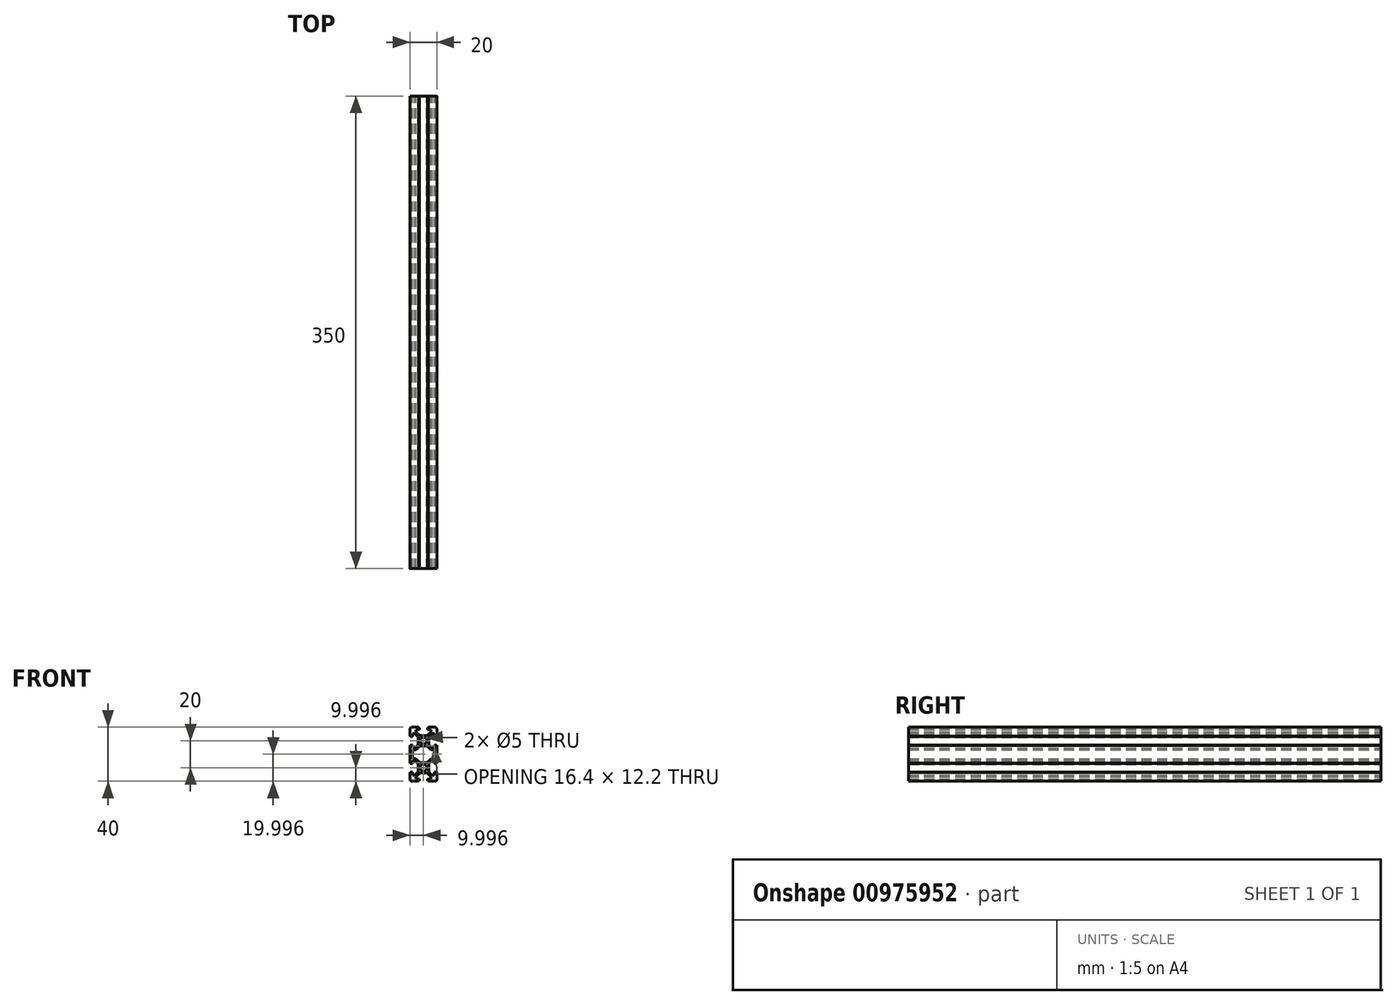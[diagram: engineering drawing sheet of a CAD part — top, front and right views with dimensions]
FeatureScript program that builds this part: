
annotation { "Feature Type Name" : "Feature", "Feature Type Description" : "" }
export const myFeature = defineFeature(function(context is Context, id is Id, definition is map)
    precondition{}
    {
        {
            var Q0;
            Q0=qCreatedBy(makeId("Front.planeOp"),FACE);
            var sketch = newSketch(context, id + "F0", { "sketchPlane" : qUnion([Q0])});
            skCircle(sketch, "E0", {"center": v(-97.48, 54.07) * mm, "radius": 2.5 * mm});
            skLineSegment(sketch, "E1.bottom", {"start": v(-88.98, 44.07) * mm, "end": v(-93.38, 44.07) * mm});
            skLineSegment(sketch, "E1.left", {"start": v(-87.48, 45.57) * mm, "end": v(-87.48, 50.47) * mm});
            skLineSegment(sketch, "E2.bottom", {"start": v(-95.47, 50.17) * mm, "end": v(-99.5, 50.17) * mm});
            skLineSegment(sketch, "E2.top", {"start": v(-95.47, 57.97) * mm, "end": v(-99.5, 57.97) * mm});
            skLineSegment(sketch, "E2.left", {"start": v(-93.58, 52.06) * mm, "end": v(-93.58, 56.08) * mm});
            skLineSegment(sketch, "E2.right", {"start": v(-101.38, 52.06) * mm, "end": v(-101.38, 56.08) * mm});
            skLineSegment(sketch, "E3.left", {"start": v(-87.48, 62.57) * mm, "end": v(-87.48, 59.57) * mm});
            skLineSegment(sketch, "E4", {"start": v(-93, 57.5) * mm, "end": v(-90.92, 59.57) * mm});
            skLineSegment(sketch, "E5.MirrorCS", {"start": v(-94.06, 58.55) * mm, "end": v(-91.98, 60.63) * mm});
            skLineSegment(sketch, "E6", {"start": v(-89.28, 59.57) * mm, "end": v(-89.28, 57.17) * mm});
            skLineSegment(sketch, "E7", {"start": v(-87.78, 57.67) * mm, "end": v(-87.48, 57.67) * mm});
            skLineSegment(sketch, "E8", {"start": v(-89.28, 57.17) * mm, "end": v(-87.98, 57.17) * mm});
            skLineSegment(sketch, "E9", {"start": v(-87.98, 57.47) * mm, "end": v(-87.98, 57.17) * mm});
            skPoint(sketch, "E10.visualSharp", {"position": v(-87.98, 57.67) * mm});
            skArc(sketch, "E10.filletArc", {"start": v(-87.78, 57.67) * mm, "mid": v(-87.93, 57.6) * mm, "end": v(-87.98, 57.47) * mm});
            skPoint(sketch, "E11.newPointA", {"position": v(-93.58, 56.9) * mm});
            skArc(sketch, "E11.filletArc", {"start": v(-93, 57.5) * mm, "mid": v(-93.43, 56.84) * mm, "end": v(-93.58, 56.08) * mm});
            skPoint(sketch, "E12.newPointA", {"position": v(-94.65, 57.97) * mm});
            skPoint(sketch, "E12.newPointB", {"position": v(-93.58, 57.97) * mm});
            skArc(sketch, "E12.filletArc", {"start": v(-95.47, 57.97) * mm, "mid": v(-94.7, 58.12) * mm, "end": v(-94.06, 58.55) * mm});
            skLineSegment(sketch, "E13.trimOffspring", {"start": v(-89.28, 59.57) * mm, "end": v(-90.92, 59.57) * mm});
            skLineSegment(sketch, "E14.MirrorCS", {"start": v(-87.78, 50.47) * mm, "end": v(-87.48, 50.47) * mm});
            skArc(sketch, "E15.MirrorCS", {"start": v(-87.78, 50.47) * mm, "mid": v(-87.93, 50.52) * mm, "end": v(-87.98, 50.67) * mm});
            skLineSegment(sketch, "E16.MirrorCS", {"start": v(-87.98, 50.67) * mm, "end": v(-87.98, 50.97) * mm});
            skArc(sketch, "E17.MirrorCS", {"start": v(-93, 50.64) * mm, "mid": v(-93.43, 51.29) * mm, "end": v(-93.58, 52.06) * mm});
            skLineSegment(sketch, "E18.MirrorCS", {"start": v(-89.28, 48.57) * mm, "end": v(-90.92, 48.57) * mm});
            skLineSegment(sketch, "E19.MirrorCS", {"start": v(-89.28, 50.97) * mm, "end": v(-87.98, 50.97) * mm});
            skLineSegment(sketch, "E20.MirrorCS", {"start": v(-88.98, 44.07) * mm, "end": v(-91.98, 44.07) * mm});
            skPoint(sketch, "E21.MirrorP", {"position": v(-87.98, 50.47) * mm});
            skLineSegment(sketch, "E22.MirrorCS", {"start": v(-94.38, 45.87) * mm, "end": v(-94.38, 44.57) * mm});
            skLineSegment(sketch, "E23.MirrorCS", {"start": v(-91.98, 45.87) * mm, "end": v(-94.38, 45.87) * mm});
            skLineSegment(sketch, "E24.MirrorCS", {"start": v(-89.28, 48.57) * mm, "end": v(-89.28, 50.97) * mm});
            skLineSegment(sketch, "E25.MirrorCS", {"start": v(-87.48, 45.57) * mm, "end": v(-87.48, 48.57) * mm});
            skLineSegment(sketch, "E26.MirrorCS", {"start": v(-93, 50.64) * mm, "end": v(-90.92, 48.57) * mm});
            skPoint(sketch, "E27.MirrorP", {"position": v(-93.58, 51.23) * mm});
            skPoint(sketch, "E28.MirrorP", {"position": v(-87.48, 44.07) * mm});
            skPoint(sketch, "E29.MirrorP", {"position": v(-93.58, 50.17) * mm});
            skLineSegment(sketch, "E30.MirrorCS", {"start": v(-94.06, 49.58) * mm, "end": v(-91.98, 47.5) * mm});
            skPoint(sketch, "E31.MirrorP", {"position": v(-94.65, 50.17) * mm});
            skArc(sketch, "E32.MirrorCS", {"start": v(-87.48, 45.57) * mm, "mid": v(-87.92, 44.5) * mm, "end": v(-88.98, 44.07) * mm});
            skLineSegment(sketch, "E33.MirrorCS", {"start": v(-91.98, 45.87) * mm, "end": v(-91.98, 47.5) * mm});
            skArc(sketch, "E34.MirrorCS", {"start": v(-95.47, 50.17) * mm, "mid": v(-94.7, 50.01) * mm, "end": v(-94.06, 49.58) * mm});
            skLineSegment(sketch, "E35.trimOffspring", {"start": v(-87.48, 57.67) * mm, "end": v(-87.48, 62.57) * mm});
            skLineSegment(sketch, "E36.MirrorCS", {"start": v(-93.88, 44.37) * mm, "end": v(-93.88, 44.07) * mm});
            skLineSegment(sketch, "E37.MirrorCS", {"start": v(-94.08, 44.57) * mm, "end": v(-94.38, 44.57) * mm});
            skLineSegment(sketch, "E38.MirrorCS", {"start": v(-93.38, 44.07) * mm, "end": v(-93.88, 44.07) * mm});
            skArc(sketch, "E39.MirrorCS", {"start": v(-93.88, 44.37) * mm, "mid": v(-93.94, 44.5) * mm, "end": v(-94.08, 44.57) * mm});
            skArc(sketch, "E40.MirrorCS", {"start": v(-107.18, 50.47) * mm, "mid": v(-107.04, 50.52) * mm, "end": v(-106.98, 50.67) * mm});
            skLineSegment(sketch, "E41.MirrorCS", {"start": v(-107.18, 57.67) * mm, "end": v(-107.48, 57.67) * mm});
            skLineSegment(sketch, "E42.MirrorCS", {"start": v(-106.98, 50.67) * mm, "end": v(-106.98, 50.97) * mm});
            skArc(sketch, "E43.MirrorCS", {"start": v(-107.18, 57.67) * mm, "mid": v(-107.04, 57.6) * mm, "end": v(-106.98, 57.47) * mm});
            skLineSegment(sketch, "E44.MirrorCS", {"start": v(-106.98, 57.47) * mm, "end": v(-106.98, 57.17) * mm});
            skLineSegment(sketch, "E45.MirrorCS", {"start": v(-107.18, 50.47) * mm, "end": v(-107.48, 50.47) * mm});
            skArc(sketch, "E46.MirrorCS", {"start": v(-107.48, 45.57) * mm, "mid": v(-107.05, 44.5) * mm, "end": v(-105.98, 44.07) * mm});
            skArc(sketch, "E47.MirrorCS", {"start": v(-101.97, 57.5) * mm, "mid": v(-101.54, 56.84) * mm, "end": v(-101.38, 56.08) * mm});
            skLineSegment(sketch, "E48.MirrorCS", {"start": v(-100.88, 44.57) * mm, "end": v(-100.58, 44.57) * mm});
            skLineSegment(sketch, "E49.MirrorCS", {"start": v(-99.5, 57.97) * mm, "end": v(-95.47, 57.97) * mm});
            skLineSegment(sketch, "E50.MirrorCS", {"start": v(-105.68, 50.97) * mm, "end": v(-106.98, 50.97) * mm});
            skLineSegment(sketch, "E51.MirrorCS", {"start": v(-105.68, 57.17) * mm, "end": v(-106.98, 57.17) * mm});
            skArc(sketch, "E52.MirrorCS", {"start": v(-101.97, 50.64) * mm, "mid": v(-101.54, 51.29) * mm, "end": v(-101.38, 52.06) * mm});
            skArc(sketch, "E53.MirrorCS", {"start": v(-101.08, 44.37) * mm, "mid": v(-101.03, 44.5) * mm, "end": v(-100.88, 44.57) * mm});
            skLineSegment(sketch, "E54.MirrorCS", {"start": v(-101.08, 44.37) * mm, "end": v(-101.08, 44.07) * mm});
            skLineSegment(sketch, "E55.MirrorCS", {"start": v(-99.5, 50.17) * mm, "end": v(-95.47, 50.17) * mm});
            skLineSegment(sketch, "E56.MirrorCS", {"start": v(-101.58, 44.07) * mm, "end": v(-101.08, 44.07) * mm});
            skLineSegment(sketch, "E57.MirrorCS", {"start": v(-100.58, 45.87) * mm, "end": v(-100.58, 44.57) * mm});
            skArc(sketch, "E58.MirrorCS", {"start": v(-99.5, 57.97) * mm, "mid": v(-100.26, 58.12) * mm, "end": v(-100.9, 58.55) * mm});
            skPoint(sketch, "E59.MirrorP", {"position": v(-107.48, 44.07) * mm});
            skLineSegment(sketch, "E60.MirrorCS", {"start": v(-105.98, 44.07) * mm, "end": v(-101.58, 44.07) * mm});
            skPoint(sketch, "E61.MirrorP", {"position": v(-101.38, 50.17) * mm});
            skArc(sketch, "E62.MirrorCS", {"start": v(-99.5, 50.17) * mm, "mid": v(-100.26, 50.01) * mm, "end": v(-100.9, 49.58) * mm});
            skPoint(sketch, "E63.MirrorP", {"position": v(-101.38, 51.23) * mm});
            skLineSegment(sketch, "E64.MirrorCS", {"start": v(-100.9, 58.55) * mm, "end": v(-102.98, 60.63) * mm});
            skPoint(sketch, "E65.MirrorP", {"position": v(-101.38, 56.9) * mm});
            skLineSegment(sketch, "E66.MirrorCS", {"start": v(-105.68, 48.57) * mm, "end": v(-105.68, 50.97) * mm});
            skLineSegment(sketch, "E67.MirrorCS", {"start": v(-101.97, 50.64) * mm, "end": v(-104.05, 48.57) * mm});
            skLineSegment(sketch, "E68.MirrorCS", {"start": v(-102.98, 45.87) * mm, "end": v(-100.58, 45.87) * mm});
            skLineSegment(sketch, "E69.MirrorCS", {"start": v(-105.68, 48.57) * mm, "end": v(-104.05, 48.57) * mm});
            skLineSegment(sketch, "E70.MirrorCS", {"start": v(-107.48, 45.57) * mm, "end": v(-107.48, 48.57) * mm});
            skLineSegment(sketch, "E71.MirrorCS", {"start": v(-107.48, 57.67) * mm, "end": v(-107.48, 62.57) * mm});
            skLineSegment(sketch, "E72.MirrorCS", {"start": v(-100.9, 49.58) * mm, "end": v(-102.98, 47.5) * mm});
            skPoint(sketch, "E73.MirrorP", {"position": v(-100.32, 50.17) * mm});
            skLineSegment(sketch, "E74.MirrorCS", {"start": v(-105.68, 59.57) * mm, "end": v(-105.68, 57.17) * mm});
            skLineSegment(sketch, "E75.MirrorCS", {"start": v(-107.48, 62.57) * mm, "end": v(-107.48, 59.57) * mm});
            skPoint(sketch, "E76.MirrorP", {"position": v(-106.98, 50.47) * mm});
            skPoint(sketch, "E77.MirrorP", {"position": v(-107.48, 64.07) * mm});
            skPoint(sketch, "E78.MirrorP", {"position": v(-106.98, 57.67) * mm});
            skLineSegment(sketch, "E79.MirrorCS", {"start": v(-101.97, 57.5) * mm, "end": v(-104.05, 59.57) * mm});
            skLineSegment(sketch, "E80.MirrorCS", {"start": v(-105.68, 59.57) * mm, "end": v(-104.05, 59.57) * mm});
            skLineSegment(sketch, "E81.MirrorCS", {"start": v(-107.48, 45.57) * mm, "end": v(-107.48, 50.47) * mm});
            skLineSegment(sketch, "E82.MirrorCS", {"start": v(-105.98, 44.07) * mm, "end": v(-102.98, 44.07) * mm});
            skPoint(sketch, "E83.MirrorP", {"position": v(-101.38, 57.97) * mm});
            skPoint(sketch, "E84.MirrorP", {"position": v(-100.32, 57.97) * mm});
            skLineSegment(sketch, "E85.MirrorCS", {"start": v(-102.98, 45.87) * mm, "end": v(-102.98, 47.5) * mm});
            skLineSegment(sketch, "E86", {"start": v(-105.68, 60.63) * mm, "end": v(-105.68, 64.07) * mm});
            skLineSegment(sketch, "E87", {"start": v(-107.48, 62.57) * mm, "end": v(-107.48, 64.07) * mm});
            skLineSegment(sketch, "E88", {"start": v(-87.48, 64.07) * mm, "end": v(-87.48, 62.57) * mm});
            skLineSegment(sketch, "E89", {"start": v(-89.28, 60.63) * mm, "end": v(-89.28, 64.07) * mm});
            skLineSegment(sketch, "E90", {"start": v(-91.98, 60.63) * mm, "end": v(-89.28, 60.63) * mm});
            skLineSegment(sketch, "E91", {"start": v(-102.98, 60.63) * mm, "end": v(-105.68, 60.63) * mm});
            skLineSegment(sketch, "E92.MirrorCS", {"start": v(-87.78, 77.67) * mm, "end": v(-87.48, 77.67) * mm});
            skLineSegment(sketch, "E93.MirrorCS", {"start": v(-87.98, 77.47) * mm, "end": v(-87.98, 77.17) * mm});
            skArc(sketch, "E94.MirrorCS", {"start": v(-87.78, 77.67) * mm, "mid": v(-87.93, 77.6) * mm, "end": v(-87.98, 77.47) * mm});
            skArc(sketch, "E95.MirrorCS", {"start": v(-87.78, 70.47) * mm, "mid": v(-87.93, 70.52) * mm, "end": v(-87.98, 70.67) * mm});
            skLineSegment(sketch, "E96.MirrorCS", {"start": v(-87.98, 70.67) * mm, "end": v(-87.98, 70.97) * mm});
            skLineSegment(sketch, "E97.MirrorCS", {"start": v(-106.98, 77.47) * mm, "end": v(-106.98, 77.17) * mm});
            skLineSegment(sketch, "E98.MirrorCS", {"start": v(-87.78, 70.47) * mm, "end": v(-87.48, 70.47) * mm});
            skArc(sketch, "E99.MirrorCS", {"start": v(-107.18, 77.67) * mm, "mid": v(-107.04, 77.6) * mm, "end": v(-106.98, 77.47) * mm});
            skLineSegment(sketch, "E100.MirrorCS", {"start": v(-107.18, 77.67) * mm, "end": v(-107.48, 77.67) * mm});
            skLineSegment(sketch, "E101.MirrorCS", {"start": v(-106.98, 70.67) * mm, "end": v(-106.98, 70.97) * mm});
            skArc(sketch, "E102.MirrorCS", {"start": v(-107.18, 70.47) * mm, "mid": v(-107.04, 70.52) * mm, "end": v(-106.98, 70.67) * mm});
            skLineSegment(sketch, "E103.MirrorCS", {"start": v(-107.18, 70.47) * mm, "end": v(-107.48, 70.47) * mm});
            skArc(sketch, "E104.MirrorCS", {"start": v(-95.47, 77.97) * mm, "mid": v(-94.7, 78.12) * mm, "end": v(-94.06, 78.55) * mm});
            skLineSegment(sketch, "E105.MirrorCS", {"start": v(-93.88, 83.77) * mm, "end": v(-93.88, 84.07) * mm});
            skArc(sketch, "E106.MirrorCS", {"start": v(-95.47, 70.17) * mm, "mid": v(-94.7, 70.01) * mm, "end": v(-94.06, 69.58) * mm});
            skLineSegment(sketch, "E107.MirrorCS", {"start": v(-89.28, 68.57) * mm, "end": v(-90.92, 68.57) * mm});
            skLineSegment(sketch, "E108.MirrorCS", {"start": v(-100.88, 83.57) * mm, "end": v(-100.58, 83.57) * mm});
            skLineSegment(sketch, "E109.MirrorCS", {"start": v(-105.68, 79.57) * mm, "end": v(-104.05, 79.57) * mm});
            skArc(sketch, "E110.MirrorCS", {"start": v(-107.48, 82.57) * mm, "mid": v(-107.05, 83.63) * mm, "end": v(-105.98, 84.07) * mm});
            skLineSegment(sketch, "E111.MirrorCS", {"start": v(-89.28, 70.97) * mm, "end": v(-87.98, 70.97) * mm});
            skLineSegment(sketch, "E112.MirrorCS", {"start": v(-101.58, 84.07) * mm, "end": v(-101.08, 84.07) * mm});
            skArc(sketch, "E113.MirrorCS", {"start": v(-101.97, 77.5) * mm, "mid": v(-101.54, 76.84) * mm, "end": v(-101.38, 76.08) * mm});
            skArc(sketch, "E114.MirrorCS", {"start": v(-87.48, 82.57) * mm, "mid": v(-87.92, 83.63) * mm, "end": v(-88.98, 84.07) * mm});
            skArc(sketch, "E115.MirrorCS", {"start": v(-99.5, 70.17) * mm, "mid": v(-100.26, 70.01) * mm, "end": v(-100.9, 69.58) * mm});
            skLineSegment(sketch, "E116.MirrorCS", {"start": v(-105.68, 77.17) * mm, "end": v(-106.98, 77.17) * mm});
            skLineSegment(sketch, "E117.MirrorCS", {"start": v(-101.08, 83.77) * mm, "end": v(-101.08, 84.07) * mm});
            skLineSegment(sketch, "E118.MirrorCS", {"start": v(-94.38, 82.27) * mm, "end": v(-94.38, 83.57) * mm});
            skLineSegment(sketch, "E119.MirrorCS", {"start": v(-93.38, 84.07) * mm, "end": v(-93.88, 84.07) * mm});
            skLineSegment(sketch, "E120.MirrorCS", {"start": v(-100.58, 82.27) * mm, "end": v(-100.58, 83.57) * mm});
            skArc(sketch, "E121.MirrorCS", {"start": v(-93, 70.64) * mm, "mid": v(-93.43, 71.29) * mm, "end": v(-93.58, 72.06) * mm});
            skArc(sketch, "E122.MirrorCS", {"start": v(-101.97, 70.64) * mm, "mid": v(-101.54, 71.29) * mm, "end": v(-101.38, 72.06) * mm});
            skLineSegment(sketch, "E123.MirrorCS", {"start": v(-89.28, 77.17) * mm, "end": v(-87.98, 77.17) * mm});
            skLineSegment(sketch, "E124.MirrorCS", {"start": v(-89.28, 79.57) * mm, "end": v(-90.92, 79.57) * mm});
            skArc(sketch, "E125.MirrorCS", {"start": v(-101.08, 83.77) * mm, "mid": v(-101.03, 83.62) * mm, "end": v(-100.88, 83.57) * mm});
            skLineSegment(sketch, "E126.MirrorCS", {"start": v(-94.08, 83.57) * mm, "end": v(-94.38, 83.57) * mm});
            skLineSegment(sketch, "E127.MirrorCS", {"start": v(-105.68, 68.57) * mm, "end": v(-104.05, 68.57) * mm});
            skLineSegment(sketch, "E128.MirrorCS", {"start": v(-105.68, 70.97) * mm, "end": v(-106.98, 70.97) * mm});
            skLineSegment(sketch, "E129.MirrorCS", {"start": v(-91.98, 82.27) * mm, "end": v(-91.98, 80.63) * mm});
            skLineSegment(sketch, "E130.MirrorCS", {"start": v(-102.98, 82.27) * mm, "end": v(-102.98, 80.63) * mm});
            skArc(sketch, "E131.MirrorCS", {"start": v(-99.5, 77.97) * mm, "mid": v(-100.26, 78.12) * mm, "end": v(-100.9, 78.55) * mm});
            skArc(sketch, "E132.MirrorCS", {"start": v(-93, 77.5) * mm, "mid": v(-93.43, 76.84) * mm, "end": v(-93.58, 76.08) * mm});
            skArc(sketch, "E133.MirrorCS", {"start": v(-93.88, 83.77) * mm, "mid": v(-93.94, 83.62) * mm, "end": v(-94.08, 83.57) * mm});
            skPoint(sketch, "E134.MirrorP", {"position": v(-97.48, 74.07) * mm});
            skLineSegment(sketch, "E135.MirrorCS", {"start": v(-101.38, 76.08) * mm, "end": v(-101.38, 72.06) * mm});
            skPoint(sketch, "E136.MirrorP", {"position": v(-101.38, 77.97) * mm});
            skLineSegment(sketch, "E137.MirrorCS", {"start": v(-88.98, 84.07) * mm, "end": v(-91.98, 84.07) * mm});
            skLineSegment(sketch, "E138.MirrorCS", {"start": v(-95.47, 70.17) * mm, "end": v(-99.5, 70.17) * mm});
            skLineSegment(sketch, "E139.MirrorCS", {"start": v(-107.48, 82.57) * mm, "end": v(-107.48, 77.67) * mm});
            skLineSegment(sketch, "E140.MirrorCS", {"start": v(-87.48, 65.57) * mm, "end": v(-87.48, 68.57) * mm});
            skPoint(sketch, "E141.MirrorP", {"position": v(-93.58, 77.97) * mm});
            skLineSegment(sketch, "E142.MirrorCS", {"start": v(-105.98, 84.07) * mm, "end": v(-101.58, 84.07) * mm});
            skLineSegment(sketch, "E143.MirrorCS", {"start": v(-87.48, 82.57) * mm, "end": v(-87.48, 79.57) * mm});
            skLineSegment(sketch, "E144.MirrorCS", {"start": v(-95.47, 77.97) * mm, "end": v(-99.5, 77.97) * mm});
            skPoint(sketch, "E145.MirrorP", {"position": v(-107.48, 84.07) * mm});
            skLineSegment(sketch, "E146.MirrorCS", {"start": v(-107.48, 65.57) * mm, "end": v(-107.48, 68.57) * mm});
            skCircle(sketch, "E147.MirrorC", {"center": v(-97.48, 74.07) * mm, "radius": 2.5 * mm});
            skPoint(sketch, "E148.MirrorP", {"position": v(-87.48, 84.07) * mm});
            skPoint(sketch, "E149.MirrorP", {"position": v(-106.98, 77.67) * mm});
            skLineSegment(sketch, "E150.MirrorCS", {"start": v(-89.28, 79.57) * mm, "end": v(-89.28, 77.17) * mm});
            skPoint(sketch, "E151.MirrorP", {"position": v(-106.98, 70.47) * mm});
            skPoint(sketch, "E152.MirrorP", {"position": v(-94.65, 77.97) * mm});
            skLineSegment(sketch, "E153.MirrorCS", {"start": v(-100.9, 78.55) * mm, "end": v(-102.98, 80.63) * mm});
            skLineSegment(sketch, "E154.MirrorCS", {"start": v(-102.98, 82.27) * mm, "end": v(-100.58, 82.27) * mm});
            skPoint(sketch, "E155.MirrorP", {"position": v(-93.58, 71.23) * mm});
            skLineSegment(sketch, "E156.MirrorCS", {"start": v(-107.48, 82.57) * mm, "end": v(-107.48, 79.57) * mm});
            skPoint(sketch, "E157.MirrorP", {"position": v(-87.98, 70.47) * mm});
            skLineSegment(sketch, "E158.MirrorCS", {"start": v(-91.98, 67.5) * mm, "end": v(-89.28, 67.5) * mm});
            skLineSegment(sketch, "E159.MirrorCS", {"start": v(-93, 77.5) * mm, "end": v(-90.92, 79.57) * mm});
            skLineSegment(sketch, "E160.MirrorCS", {"start": v(-102.98, 67.5) * mm, "end": v(-105.68, 67.5) * mm});
            skLineSegment(sketch, "E161.MirrorCS", {"start": v(-91.98, 82.27) * mm, "end": v(-94.38, 82.27) * mm});
            skLineSegment(sketch, "E162.MirrorCS", {"start": v(-105.68, 79.57) * mm, "end": v(-105.68, 77.17) * mm});
            skPoint(sketch, "E163.MirrorP", {"position": v(-101.38, 76.9) * mm});
            skPoint(sketch, "E164.MirrorP", {"position": v(-93.58, 70.17) * mm});
            skLineSegment(sketch, "E165.MirrorCS", {"start": v(-99.5, 77.97) * mm, "end": v(-95.47, 77.97) * mm});
            skLineSegment(sketch, "E166.MirrorCS", {"start": v(-105.98, 84.07) * mm, "end": v(-102.98, 84.07) * mm});
            skPoint(sketch, "E167.MirrorP", {"position": v(-100.32, 70.17) * mm});
            skLineSegment(sketch, "E168.MirrorCS", {"start": v(-99.5, 70.17) * mm, "end": v(-95.47, 70.17) * mm});
            skPoint(sketch, "E169.MirrorP", {"position": v(-101.38, 71.23) * mm});
            skLineSegment(sketch, "E170.MirrorCS", {"start": v(-87.48, 82.57) * mm, "end": v(-87.48, 77.67) * mm});
            skPoint(sketch, "E171.MirrorP", {"position": v(-93.58, 76.9) * mm});
            skLineSegment(sketch, "E172.MirrorCS", {"start": v(-101.97, 77.5) * mm, "end": v(-104.05, 79.57) * mm});
            skPoint(sketch, "E173.MirrorP", {"position": v(-100.32, 77.97) * mm});
            skLineSegment(sketch, "E174.MirrorCS", {"start": v(-93, 70.64) * mm, "end": v(-90.92, 68.57) * mm});
            skLineSegment(sketch, "E175.MirrorCS", {"start": v(-94.06, 78.55) * mm, "end": v(-91.98, 80.63) * mm});
            skLineSegment(sketch, "E176.MirrorCS", {"start": v(-107.48, 70.47) * mm, "end": v(-107.48, 65.57) * mm});
            skPoint(sketch, "E177.MirrorP", {"position": v(-101.38, 70.17) * mm});
            skLineSegment(sketch, "E178.MirrorCS", {"start": v(-94.06, 69.58) * mm, "end": v(-91.98, 67.5) * mm});
            skLineSegment(sketch, "E179.MirrorCS", {"start": v(-105.68, 68.57) * mm, "end": v(-105.68, 70.97) * mm});
            skPoint(sketch, "E180.MirrorP", {"position": v(-94.65, 70.17) * mm});
            skLineSegment(sketch, "E181.MirrorCS", {"start": v(-100.9, 69.58) * mm, "end": v(-102.98, 67.5) * mm});
            skLineSegment(sketch, "E182.MirrorCS", {"start": v(-89.28, 68.57) * mm, "end": v(-89.28, 70.97) * mm});
            skPoint(sketch, "E183.MirrorP", {"position": v(-87.98, 77.67) * mm});
            skLineSegment(sketch, "E184.MirrorCS", {"start": v(-87.48, 70.47) * mm, "end": v(-87.48, 65.57) * mm});
            skLineSegment(sketch, "E185.MirrorCS", {"start": v(-101.97, 70.64) * mm, "end": v(-104.05, 68.57) * mm});
            skLineSegment(sketch, "E186.MirrorCS", {"start": v(-93.58, 76.08) * mm, "end": v(-93.58, 72.06) * mm});
            skLineSegment(sketch, "E187.MirrorCS", {"start": v(-88.98, 84.07) * mm, "end": v(-93.38, 84.07) * mm});
            skLineSegment(sketch, "E188.MirrorCS", {"start": v(-89.28, 67.5) * mm, "end": v(-89.28, 64.07) * mm});
            skLineSegment(sketch, "E189.MirrorCS", {"start": v(-87.48, 64.07) * mm, "end": v(-87.48, 65.57) * mm});
            skLineSegment(sketch, "E190.MirrorCS", {"start": v(-105.68, 67.5) * mm, "end": v(-105.68, 64.07) * mm});
            skLineSegment(sketch, "E191.MirrorCS", {"start": v(-107.48, 65.57) * mm, "end": v(-107.48, 64.07) * mm});
            skSolve(sketch);
        }
        {
            var Q0;
            Q0=makeQuery(id+"F0.imprint","IMPRINT",FACE,{"disambiguationData":[TD([[makeQuery(id+"F0.imprint","IMPRINT",EDGE,{"derivedFrom":sQuery(id+"F0.wireOp",EDGE,"E1.bottom")}),-1.0]])]});
            extrude(context, id + "F1", {"entities" : qUnion([Q0]), "depth" : 350 * mm, "offsetDistance" : 25 * mm});
        }
    });
